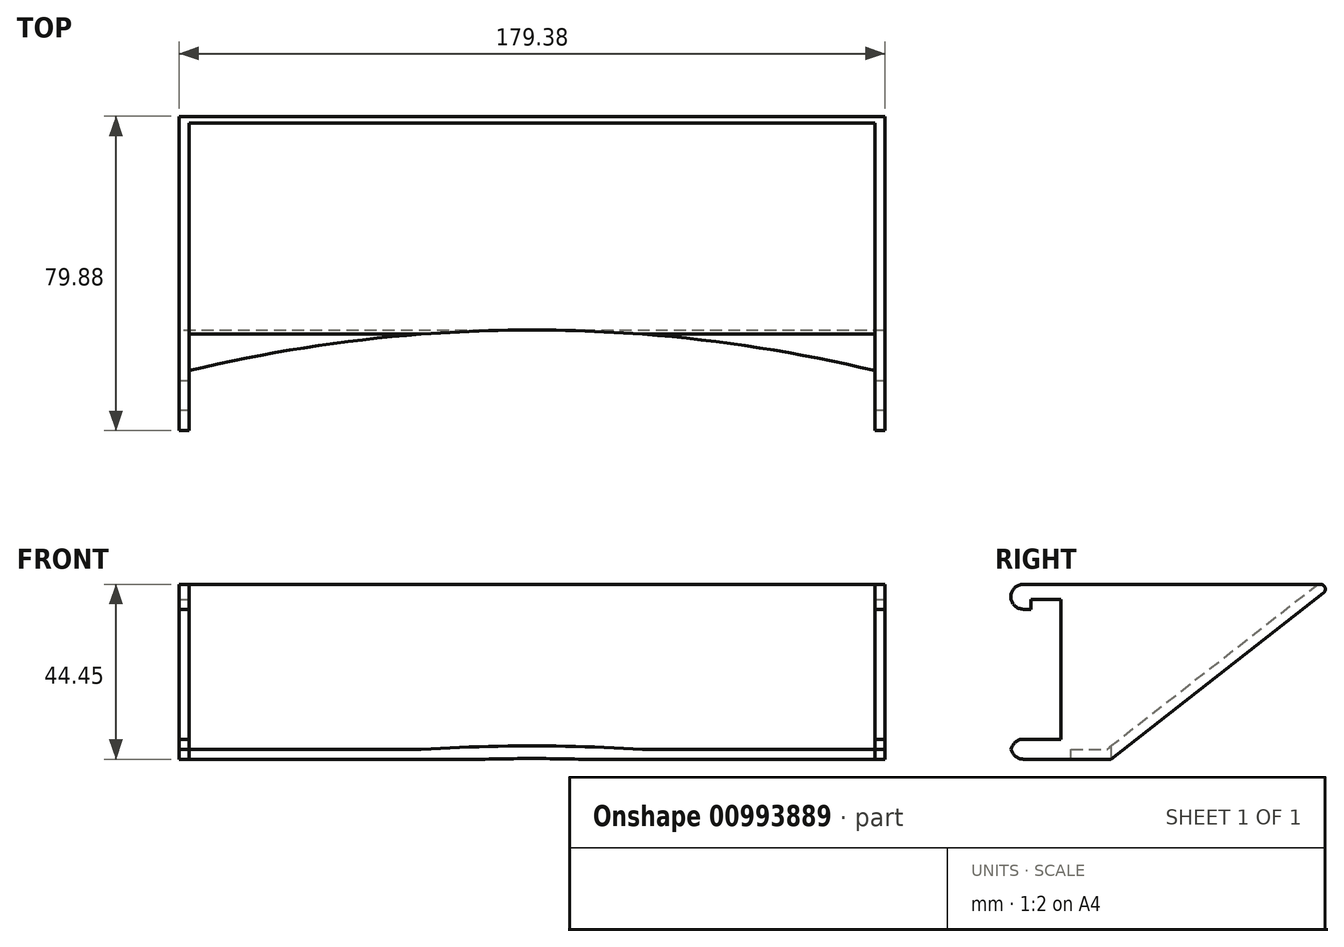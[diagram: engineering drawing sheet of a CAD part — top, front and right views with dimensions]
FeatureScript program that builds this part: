
annotation { "Feature Type Name" : "Feature", "Feature Type Description" : "" }
export const myFeature = defineFeature(function(context is Context, id is Id, definition is map)
    precondition{}
    {
        {
            var Q0;
            Q0=qCreatedBy(makeId("Right.planeOp"),FACE);
            var sketch = newSketch(context, id + "F0", { "sketchPlane" : qUnion([Q0])});
            skLineSegment(sketch, "E0", {"start": v(0, 0) * mm, "end": v(0, 44.45) * mm});
            skLineSegment(sketch, "E1", {"start": v(0, 44.45) * mm, "end": v(56.9, 44.45) * mm});
            skLineSegment(sketch, "E2", {"start": v(56.9, 44.45) * mm, "end": v(0, 0) * mm});
            skLineSegment(sketch, "E3", {"start": v(0, 0) * mm, "end": v(24.87, 0) * mm, "construction": true});
            skSolve(sketch);
        }
        {
            var Q0;
            Q0 = qSketchRegion(id + "F0", true);
            extrude(context, id + "F1", {"entities" : qUnion([Q0]), "endBound" : BoundingType.SYMMETRIC, "depth" : 179.39 * mm, "offsetDistance" : 25.4 * mm});
        }
        {
            var Q0;
            Q0=makeQuery(id+"F1.opExtrude","SWEPT_FACE",FACE,{"disambiguationData":[OSD([sQuery(id+"F0.wireOp",EDGE,"E0")])]});
            extrude(context, id + "F2", {"entities" : qUnion([Q0]), "operationType" : NewBodyOperationType.ADD, "depth" : 12.7 * mm, "offsetDistance" : 25.4 * mm});
        }
        {
            var Q0;
            {var subQ0=sQuery(id+"F0.wireOp",EDGE,"E1");Q0=makeQuery(id+"F2.boolean.opBoolean","MERGE",FACE,{"derivedFrom":[makeQuery(id+"F1.opExtrude","SWEPT_FACE",FACE,{"disambiguationData":[OSD([subQ0])]}),makeQuery(id+"F2.opExtrude","SWEPT_FACE",FACE,{"disambiguationData":[OSD([sQuery(id+"F0.wireOp",EDGE,"E0"),subQ0])]})]});}
            var sketch = newSketch(context, id + "F3", { "sketchPlane" : qUnion([Q0])});
            skLineSegment(sketch, "E4", {"start": v(-87.15, -12.7) * mm, "end": v(87.15, -12.7) * mm});
            skLineSegment(sketch, "E5", {"start": v(-87.15, -12.7) * mm, "end": v(-87.15, -10.16) * mm});
            skLineSegment(sketch, "E6", {"start": v(87.15, -12.7) * mm, "end": v(87.15, -10.16) * mm});
            skArc(sketch, "E7", {"start": v(87.15, -10.16) * mm, "mid": v(0, 0.2) * mm, "end": v(-87.15, -10.16) * mm});
            skSolve(sketch);
        }
        {
            var Q0;
            Q0=makeQuery(id+"F3.imprint","IMPRINT",FACE,{"disambiguationData":[TD([[makeQuery(id+"F3.imprint","IMPRINT",EDGE,{"derivedFrom":sQuery(id+"F3.wireOp",EDGE,"E4")}),-1.0]])]});
            extrude(context, id + "F4", {"entities" : qUnion([Q0]), "operationType" : NewBodyOperationType.REMOVE, "endBound" : BoundingType.THROUGH_ALL, "oppositeDirection" : true, "depth" : 25.4 * mm, "offsetDistance" : 25.4 * mm});
        }
        {
            var Q0;
            Q0=makeQuery(id+"F4.boolean.opBoolean","COPY",FACE,{"derivedFrom":makeQuery(id+"F4.opExtrude","SWEPT_FACE",FACE,{"disambiguationData":[OSD([sQuery(id+"F3.wireOp",EDGE,"w3iMEGZt-yHUm-9SDC-SKcr-fGB3f0vRGBhc")])]})});
            var Q1;
            {var subQ0=sQuery(id+"F0.wireOp",EDGE,"E1");Q1=makeQuery(id+"F2.boolean.opBoolean","MERGE",FACE,{"derivedFrom":[makeQuery(id+"F1.opExtrude","SWEPT_FACE",FACE,{"disambiguationData":[OSD([subQ0])]}),makeQuery(id+"F2.opExtrude","SWEPT_FACE",FACE,{"disambiguationData":[OSD([sQuery(id+"F0.wireOp",EDGE,"E0"),subQ0])]})]});}
            var Q2;
            Q2=makeQuery(id+"F4.boolean.opBoolean","COPY",FACE,{"derivedFrom":makeQuery(id+"F4.opExtrude","SWEPT_FACE",FACE,{"disambiguationData":[OSD([sQuery(id+"F3.wireOp",EDGE,"7iGFMPCt-OrQo-QgIq-eDfj-S4QJKakwyO3F")])]})});
            var Q3;
            Q3=makeQuery(id+"F4.boolean.opBoolean","COPY",FACE,{"derivedFrom":makeQuery(id+"F4.opExtrude","SWEPT_FACE",FACE,{"disambiguationData":[OSD([sQuery(id+"F3.wireOp",EDGE,"E7")])]})});
            shell(context, id + "F5", {"entities" : qUnion([Q0, Q1, Q2, Q3]), "thickness" : 2.54 * mm});
        }
        {
            var Q0;
            Q0=makeQuery(id+"F1.opExtrude","SWEPT_EDGE",EDGE,{"disambiguationData":[OSD([sQuery(id+"F0.wireOp",EDGE,"E1"),sQuery(id+"F0.wireOp",EDGE,"E2")])]});
            fillet(context, id + "F6", {"entities" : qUnion([Q0]), "radius" : 1.27 * mm, "tangentPropagation" : true, "allowEdgeOverflow" : false});
        }
        {
            var Q0;
            {var subQ1=sQuery(id+"F0.wireOp",EDGE,"E0");Q0=makeQuery(id+"F4.boolean.opBoolean","SPLIT",FACE,{"disambiguationData":[TD([makeQuery(id+"F4.opExtrude","SWEPT_FACE",FACE,{"disambiguationData":[OSD([sQuery(id+"F3.wireOp",EDGE,"E5")])]})])],"derivedFrom":makeQuery(id+"F2.opExtrude","CAP_FACE",FACE,{"disambiguationData":[OSD([subQ1])],"isStart":false})});}
            var sketch = newSketch(context, id + "F7", { "sketchPlane" : qUnion([Q0])});
            skLineSegment(sketch, "E8.bottom", {"start": v(-89.7, 44.45) * mm, "end": v(-87.15, 44.45) * mm});
            skLineSegment(sketch, "E8.top", {"start": v(-89.7, 40.64) * mm, "end": v(-87.15, 40.64) * mm});
            skLineSegment(sketch, "E8.left", {"start": v(-89.7, 44.45) * mm, "end": v(-89.7, 40.64) * mm});
            skLineSegment(sketch, "E8.right", {"start": v(-87.15, 44.45) * mm, "end": v(-87.15, 40.64) * mm});
            skLineSegment(sketch, "E9.bottom", {"start": v(-89.7, 0) * mm, "end": v(-87.15, 0) * mm});
            skLineSegment(sketch, "E9.top", {"start": v(-89.7, 5.08) * mm, "end": v(-87.15, 5.08) * mm});
            skLineSegment(sketch, "E9.left", {"start": v(-89.7, 0) * mm, "end": v(-89.7, 5.08) * mm});
            skLineSegment(sketch, "E9.right", {"start": v(-87.15, 0) * mm, "end": v(-87.15, 5.08) * mm});
            skSolve(sketch);
        }
        {
            var Q0;
            {var subQ1=sQuery(id+"F0.wireOp",EDGE,"E0");Q0=makeQuery(id+"F4.boolean.opBoolean","SPLIT",FACE,{"disambiguationData":[TD([makeQuery(id+"F4.opExtrude","SWEPT_FACE",FACE,{"disambiguationData":[OSD([sQuery(id+"F3.wireOp",EDGE,"E6")])]})])],"derivedFrom":makeQuery(id+"F2.opExtrude","CAP_FACE",FACE,{"disambiguationData":[OSD([subQ1])],"isStart":false})});}
            var sketch = newSketch(context, id + "F8", { "sketchPlane" : qUnion([Q0])});
            skLineSegment(sketch, "E10.bottom", {"start": v(87.15, 44.45) * mm, "end": v(89.7, 44.45) * mm});
            skLineSegment(sketch, "E10.top", {"start": v(87.15, 40.64) * mm, "end": v(89.7, 40.64) * mm});
            skLineSegment(sketch, "E10.left", {"start": v(87.15, 44.45) * mm, "end": v(87.15, 40.64) * mm});
            skLineSegment(sketch, "E10.right", {"start": v(89.7, 44.45) * mm, "end": v(89.7, 40.64) * mm});
            skLineSegment(sketch, "E11.bottom", {"start": v(87.15, 0) * mm, "end": v(89.7, 0) * mm});
            skLineSegment(sketch, "E11.top", {"start": v(87.15, 5.08) * mm, "end": v(89.7, 5.08) * mm});
            skLineSegment(sketch, "E11.left", {"start": v(87.15, 0) * mm, "end": v(87.15, 5.08) * mm});
            skLineSegment(sketch, "E11.right", {"start": v(89.7, 0) * mm, "end": v(89.7, 5.08) * mm});
            skSolve(sketch);
        }
        {
            var Q0;
            Q0 = qSketchRegion(id + "F7", true);
            var Q1;
            Q1 = qSketchRegion(id + "F8", true);
            extrude(context, id + "F9", {"entities" : qUnion([Q0, Q1]), "operationType" : NewBodyOperationType.ADD, "depth" : 12.7 * mm, "offsetDistance" : 25.4 * mm});
        }
        {
            var Q0;
            Q0=makeQuery(id+"F9.opExtrude","SWEPT_FACE",FACE,{"disambiguationData":[OSD([sQuery(id+"F8.wireOp",EDGE,"E10.top")])]});
            var sketch = newSketch(context, id + "F10", { "sketchPlane" : qUnion([Q0])});
            skLineSegment(sketch, "E12.bottom", {"start": v(89.7, 25.4) * mm, "end": v(87.15, 25.4) * mm});
            skLineSegment(sketch, "E12.top", {"start": v(89.7, 20.32) * mm, "end": v(87.15, 20.32) * mm});
            skLineSegment(sketch, "E12.left", {"start": v(89.7, 25.4) * mm, "end": v(89.7, 20.32) * mm});
            skLineSegment(sketch, "E12.right", {"start": v(87.15, 25.4) * mm, "end": v(87.15, 20.32) * mm});
            skSolve(sketch);
        }
        {
            var Q0;
            Q0=makeQuery(id+"F9.opExtrude","SWEPT_FACE",FACE,{"disambiguationData":[OSD([sQuery(id+"F7.wireOp",EDGE,"E8.top")])]});
            var sketch = newSketch(context, id + "F11", { "sketchPlane" : qUnion([Q0])});
            skLineSegment(sketch, "E13.bottom", {"start": v(-87.15, 25.4) * mm, "end": v(-89.7, 25.4) * mm});
            skLineSegment(sketch, "E13.top", {"start": v(-87.15, 20.32) * mm, "end": v(-89.7, 20.32) * mm});
            skLineSegment(sketch, "E13.left", {"start": v(-87.15, 25.4) * mm, "end": v(-87.15, 20.32) * mm});
            skLineSegment(sketch, "E13.right", {"start": v(-89.7, 25.4) * mm, "end": v(-89.7, 20.32) * mm});
            skSolve(sketch);
        }
        {
            var Q0;
            Q0 = qSketchRegion(id + "F11", true);
            var Q1;
            Q1 = qSketchRegion(id + "F10", true);
            extrude(context, id + "F12", {"entities" : qUnion([Q0, Q1]), "operationType" : NewBodyOperationType.ADD, "depth" : 2.54 * mm, "offsetDistance" : 25.4 * mm});
        }
        {
            var Q0;
            Q0=makeQuery(id+"F9.opExtrude","CAP_EDGE",EDGE,{"disambiguationData":[OSD([sQuery(id+"F8.wireOp",EDGE,"E10.bottom")])],"isStart":false});
            var Q1;
            Q1=makeQuery(id+"F12.opExtrude","CAP_EDGE",EDGE,{"disambiguationData":[OSD([sQuery(id+"F10.wireOp",EDGE,"E12.bottom")])],"isStart":false});
            var Q2;
            Q2=makeQuery(id+"F9.opExtrude","CAP_EDGE",EDGE,{"disambiguationData":[OSD([sQuery(id+"F7.wireOp",EDGE,"E8.bottom")])],"isStart":false});
            var Q3;
            Q3=makeQuery(id+"F12.opExtrude","CAP_EDGE",EDGE,{"disambiguationData":[OSD([sQuery(id+"F11.wireOp",EDGE,"E13.bottom")])],"isStart":false});
            var Q4;
            Q4=makeQuery(id+"F9.opExtrude","CAP_EDGE",EDGE,{"disambiguationData":[OSD([sQuery(id+"F7.wireOp",EDGE,"E9.top")])],"isStart":false});
            var Q5;
            Q5=makeQuery(id+"F9.opExtrude","CAP_EDGE",EDGE,{"disambiguationData":[OSD([sQuery(id+"F7.wireOp",EDGE,"E9.bottom")])],"isStart":false});
            var Q6;
            Q6=makeQuery(id+"F9.opExtrude","CAP_EDGE",EDGE,{"disambiguationData":[OSD([sQuery(id+"F8.wireOp",EDGE,"E11.top")])],"isStart":false});
            var Q7;
            Q7=makeQuery(id+"F9.opExtrude","CAP_EDGE",EDGE,{"disambiguationData":[OSD([sQuery(id+"F8.wireOp",EDGE,"E11.bottom")])],"isStart":false});
            fillet(context, id + "F13", {"entities" : qUnion([Q0, Q1, Q2, Q3, Q4, Q5, Q6, Q7]), "radius" : 3.17 * mm, "tangentPropagation" : true, "allowEdgeOverflow" : false});
        }
    });
